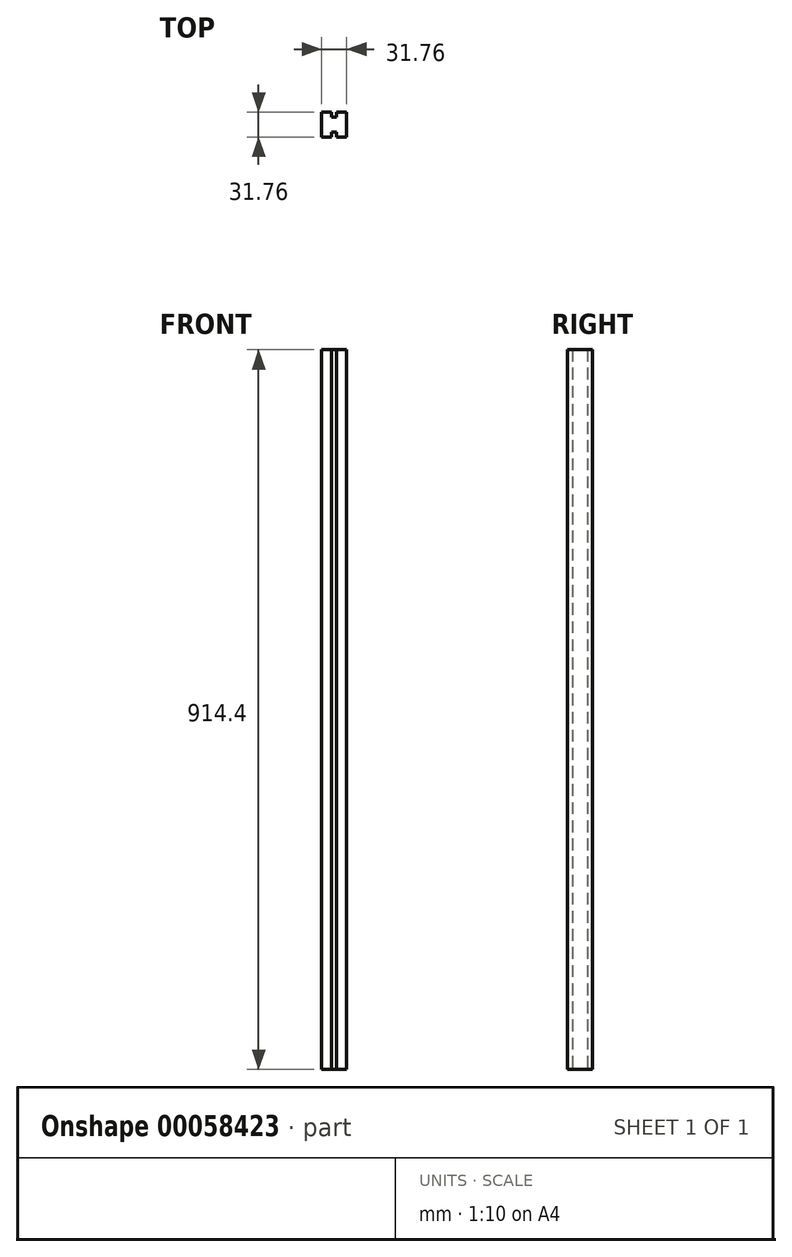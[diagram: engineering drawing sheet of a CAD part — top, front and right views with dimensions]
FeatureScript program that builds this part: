
annotation { "Feature Type Name" : "Feature", "Feature Type Description" : "" }
export const myFeature = defineFeature(function(context is Context, id is Id, definition is map)
    precondition{}
    {
        {
            var Q0;
            Q0=qCreatedBy(makeId("Top.planeOp"),FACE);
            var sketch = newSketch(context, id + "F0", { "sketchPlane" : qUnion([Q0])});
            skLineSegment(sketch, "E0.rect.bottom", {"start": v(15.88, -15.87) * mm, "end": v(3.18, -15.88) * mm});
            skLineSegment(sketch, "E0.rect.top", {"start": v(15.87, 15.88) * mm, "end": v(3.17, 15.87) * mm});
            skLineSegment(sketch, "E0.rect.left", {"start": v(15.88, -15.87) * mm, "end": v(15.87, 15.88) * mm});
            skLineSegment(sketch, "E0.rect.right", {"start": v(-15.87, -15.88) * mm, "end": v(-15.88, 15.87) * mm});
            skPoint(sketch, "E0.rect.middle", {"position": v(0, 0) * mm});
            skLineSegment(sketch, "E1", {"start": v(-3.18, 15.87) * mm, "end": v(-3.18, 9.52) * mm});
            skLineSegment(sketch, "E2", {"start": v(-3.18, 9.52) * mm, "end": v(3.17, 9.52) * mm});
            skLineSegment(sketch, "E3", {"start": v(3.17, 9.52) * mm, "end": v(3.17, 15.87) * mm});
            skLineSegment(sketch, "E4", {"start": v(-3.17, -15.88) * mm, "end": v(-3.17, -9.53) * mm});
            skLineSegment(sketch, "E5", {"start": v(-3.17, -9.53) * mm, "end": v(3.18, -9.52) * mm});
            skLineSegment(sketch, "E6", {"start": v(3.18, -9.53) * mm, "end": v(3.18, -15.88) * mm});
            skLineSegment(sketch, "E7", {"start": v(0, 9.52) * mm, "end": v(0, -9.53) * mm, "construction": true});
            skLineSegment(sketch, "E8.trimOffspring", {"start": v(-3.18, 15.87) * mm, "end": v(-15.88, 15.87) * mm});
            skLineSegment(sketch, "E9.trimOffspring", {"start": v(-3.17, -15.88) * mm, "end": v(-15.87, -15.88) * mm});
            skSolve(sketch);
        }
        {
            var Q0;
            Q0=qSketchRegion(id+"F0",true);
            extrude(context, id + "F1", {"entities" : qUnion([Q0]), "depth" : 914.4 * mm});
        }
    });
